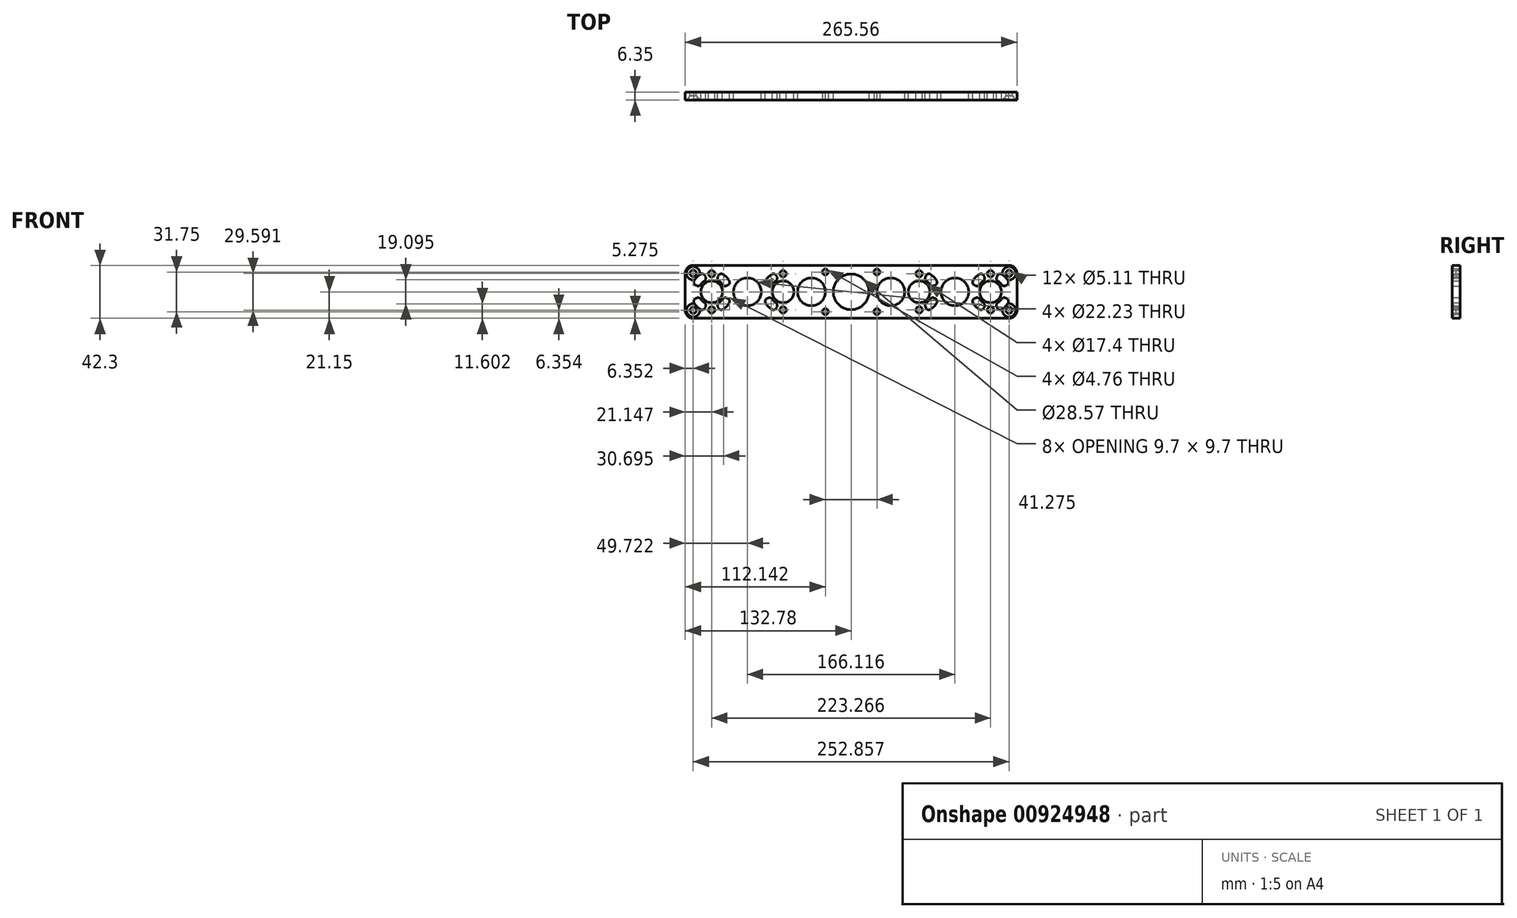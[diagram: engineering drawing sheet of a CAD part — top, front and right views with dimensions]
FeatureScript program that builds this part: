
annotation { "Feature Type Name" : "Feature", "Feature Type Description" : "" }
export const myFeature = defineFeature(function(context is Context, id is Id, definition is map)
    precondition{}
    {
        {
            var Q0;
            Q0=qCreatedBy(makeId("Front.planeOp"),FACE);
            var sketch = newSketch(context, id + "F0", { "sketchPlane" : qUnion([Q0])});
            skLineSegment(sketch, "E0.bottom", {"start": v(-139.7, 25.4) * mm, "end": v(139.7, 25.4) * mm, "construction": true});
            skLineSegment(sketch, "E0.top", {"start": v(-139.7, -25.4) * mm, "end": v(139.7, -25.4) * mm, "construction": true});
            skLineSegment(sketch, "E0.left", {"start": v(-139.7, 25.4) * mm, "end": v(-139.7, -25.4) * mm, "construction": true});
            skLineSegment(sketch, "E0.right", {"start": v(139.7, 25.4) * mm, "end": v(139.7, -25.4) * mm, "construction": true});
            skPoint(sketch, "E0.middle", {"position": v(0, 0) * mm});
            skCircle(sketch, "E1", {"center": v(-111.63, 0) * mm, "radius": 21.15 * mm, "construction": true});
            skCircle(sketch, "E2", {"center": v(-54.48, 0) * mm, "radius": 21.15 * mm, "construction": true});
            skCircle(sketch, "E3", {"center": v(-111.63, 0) * mm, "radius": 4.76 * mm, "construction": true});
            skCircle(sketch, "E4", {"center": v(-83.06, 0) * mm, "radius": 23.81 * mm, "construction": true});
            skCircle(sketch, "E5", {"center": v(-54.48, 0) * mm, "radius": 4.76 * mm, "construction": true});
            skCircle(sketch, "E6", {"center": v(-83.06, 0) * mm, "radius": 19.09 * mm, "construction": true});
            skCircle(sketch, "E7", {"center": v(-31.75, 0) * mm, "radius": 19.09 * mm, "construction": true});
            skCircle(sketch, "E8", {"center": v(-83.06, 0) * mm, "radius": 11.11 * mm});
            skCircle(sketch, "E9", {"center": v(-31.75, 0) * mm, "radius": 8.9 * mm, "construction": true});
            skCircle(sketch, "E10", {"center": v(0, 0) * mm, "radius": 22.86 * mm, "construction": true});
            skLineSegment(sketch, "E11", {"start": v(0, 25.4) * mm, "end": v(0, -25.4) * mm, "construction": true});
            skCircle(sketch, "E12.MirrorC", {"center": v(54.48, 0) * mm, "radius": 21.15 * mm, "construction": true});
            skCircle(sketch, "E13.MirrorC", {"center": v(111.63, 0) * mm, "radius": 21.15 * mm, "construction": true});
            skCircle(sketch, "E14.MirrorC", {"center": v(111.63, 0) * mm, "radius": 4.76 * mm, "construction": true});
            skCircle(sketch, "E15.MirrorC", {"center": v(83.06, 0) * mm, "radius": 19.09 * mm, "construction": true});
            skCircle(sketch, "E16.MirrorC", {"center": v(83.06, 0) * mm, "radius": 11.11 * mm});
            skCircle(sketch, "E17.MirrorC", {"center": v(54.48, 0) * mm, "radius": 4.76 * mm, "construction": true});
            skCircle(sketch, "E18.MirrorC", {"center": v(83.06, 0) * mm, "radius": 23.81 * mm, "construction": true});
            skCircle(sketch, "E19.MirrorC", {"center": v(31.75, 0) * mm, "radius": 19.09 * mm, "construction": true});
            skCircle(sketch, "E20.MirrorC", {"center": v(31.75, 0) * mm, "radius": 8.9 * mm, "construction": true});
            skLineSegment(sketch, "E21", {"start": v(-111.63, 14.5) * mm, "end": v(-111.63, 0) * mm, "construction": true});
            skLineSegment(sketch, "E22", {"start": v(-111.63, 0) * mm, "end": v(-111.63, -14.5) * mm, "construction": true});
            skCircle(sketch, "E23", {"center": v(-111.63, 14.5) * mm, "radius": 2.55 * mm});
            skCircle(sketch, "E24", {"center": v(-111.63, -14.5) * mm, "radius": 2.55 * mm});
            skCircle(sketch, "E25", {"center": v(-111.63, 0) * mm, "radius": 8.7 * mm});
            skLineSegment(sketch, "E26", {"start": v(-54.48, -14.5) * mm, "end": v(-54.48, 0) * mm, "construction": true});
            skLineSegment(sketch, "E27", {"start": v(-54.48, 0) * mm, "end": v(-54.48, 14.5) * mm, "construction": true});
            skCircle(sketch, "E28", {"center": v(-54.48, 14.5) * mm, "radius": 2.55 * mm});
            skCircle(sketch, "E29", {"center": v(-54.48, -14.5) * mm, "radius": 2.55 * mm});
            skCircle(sketch, "E30", {"center": v(-54.48, 0) * mm, "radius": 8.7 * mm});
            skLineSegment(sketch, "E31.MirrorCS", {"start": v(54.48, 0) * mm, "end": v(54.48, 14.5) * mm, "construction": true});
            skCircle(sketch, "E32.MirrorC", {"center": v(54.48, 14.5) * mm, "radius": 2.55 * mm});
            skLineSegment(sketch, "E33.MirrorCS", {"start": v(54.48, -14.5) * mm, "end": v(54.48, 0) * mm, "construction": true});
            skCircle(sketch, "E34.MirrorC", {"center": v(54.48, -14.5) * mm, "radius": 2.55 * mm});
            skCircle(sketch, "E35.MirrorC", {"center": v(54.48, 0) * mm, "radius": 8.7 * mm});
            skCircle(sketch, "E36.MirrorC", {"center": v(111.63, 0) * mm, "radius": 8.7 * mm});
            skLineSegment(sketch, "E37.MirrorCS", {"start": v(111.63, 0) * mm, "end": v(111.63, -14.5) * mm, "construction": true});
            skCircle(sketch, "E38.MirrorC", {"center": v(111.63, -14.5) * mm, "radius": 2.55 * mm});
            skLineSegment(sketch, "E39.MirrorCS", {"start": v(111.63, 14.5) * mm, "end": v(111.63, 0) * mm, "construction": true});
            skCircle(sketch, "E40.MirrorC", {"center": v(111.63, 14.5) * mm, "radius": 2.55 * mm});
            skCircle(sketch, "E41", {"center": v(-31.75, 0) * mm, "radius": 11.11 * mm});
            skCircle(sketch, "E42", {"center": v(31.75, 0) * mm, "radius": 11.11 * mm});
            skCircle(sketch, "E43", {"center": v(0, 0) * mm, "radius": 14.29 * mm});
            skArc(sketch, "E44", {"start": v(-111.63, 21.15) * mm, "mid": v(-132.78, 0) * mm, "end": v(-111.63, -21.15) * mm, "construction": true});
            skLineSegment(sketch, "E45", {"start": v(-111.63, 21.15) * mm, "end": v(111.63, 21.15) * mm});
            skArc(sketch, "E46", {"start": v(111.63, 21.15) * mm, "mid": v(132.78, 0) * mm, "end": v(111.63, -21.15) * mm, "construction": true});
            skLineSegment(sketch, "E47", {"start": v(111.63, -21.15) * mm, "end": v(-111.63, -21.15) * mm});
            skLineSegment(sketch, "E48", {"start": v(111.63, 21.15) * mm, "end": v(126.43, 21.15) * mm});
            skPoint(sketch, "E48.endSnap0", {"position": v(132.78, 0) * mm});
            skLineSegment(sketch, "E49", {"start": v(132.78, 14.8) * mm, "end": v(132.78, -14.8) * mm});
            skLineSegment(sketch, "E50", {"start": v(126.43, -21.15) * mm, "end": v(111.63, -21.15) * mm});
            skCircle(sketch, "E51", {"center": v(126.43, 14.8) * mm, "radius": 6.35 * mm, "construction": true});
            skCircle(sketch, "E52", {"center": v(126.43, 14.8) * mm, "radius": 2.55 * mm});
            skLineSegment(sketch, "E53", {"start": v(-111.63, -21.15) * mm, "end": v(-126.43, -21.15) * mm});
            skPoint(sketch, "E53.endSnap0", {"position": v(-132.78, 0) * mm});
            skLineSegment(sketch, "E54", {"start": v(-132.78, -14.8) * mm, "end": v(-132.78, 14.8) * mm});
            skLineSegment(sketch, "E55", {"start": v(-126.43, 21.15) * mm, "end": v(-111.63, 21.15) * mm});
            skPoint(sketch, "E56.visualSharp", {"position": v(132.78, 21.15) * mm});
            skArc(sketch, "E56.filletArc", {"start": v(132.78, 14.8) * mm, "mid": v(130.92, 19.29) * mm, "end": v(126.43, 21.15) * mm});
            skPoint(sketch, "E57.visualSharp", {"position": v(132.78, -21.15) * mm});
            skArc(sketch, "E57.filletArc", {"start": v(126.43, -21.15) * mm, "mid": v(130.92, -19.29) * mm, "end": v(132.78, -14.8) * mm});
            skPoint(sketch, "E58.visualSharp", {"position": v(-132.78, -21.15) * mm});
            skArc(sketch, "E58.filletArc", {"start": v(-132.78, -14.8) * mm, "mid": v(-130.92, -19.29) * mm, "end": v(-126.43, -21.15) * mm});
            skPoint(sketch, "E59.visualSharp", {"position": v(-132.78, 21.15) * mm});
            skArc(sketch, "E59.filletArc", {"start": v(-126.43, 21.15) * mm, "mid": v(-130.92, 19.29) * mm, "end": v(-132.78, 14.8) * mm});
            skCircle(sketch, "E60", {"center": v(-126.43, 14.8) * mm, "radius": 6.35 * mm, "construction": true});
            skCircle(sketch, "E61", {"center": v(126.43, -14.8) * mm, "radius": 6.35 * mm, "construction": true});
            skCircle(sketch, "E62", {"center": v(126.43, -14.8) * mm, "radius": 2.55 * mm});
            skCircle(sketch, "E63", {"center": v(-126.43, -14.8) * mm, "radius": 6.35 * mm, "construction": true});
            skCircle(sketch, "E64", {"center": v(-126.43, -14.8) * mm, "radius": 2.55 * mm});
            skCircle(sketch, "E65", {"center": v(-126.43, 14.8) * mm, "radius": 2.55 * mm});
            skSolve(sketch);
        }
        {
            var Q0;
            Q0=qSketchRegion(id+"F0",true);
            extrude(context, id + "F1", {"entities" : qUnion([Q0]), "depth" : 6.35 * mm, "offsetDistance" : 25.4 * mm});
        }
        {
            var Q0;
            Q0=makeQuery(id+"F1.opExtrude","CAP_FACE",FACE,{"disambiguationData":[OSD([sQuery(id+"F0.wireOp",EDGE,"E8"),sQuery(id+"F0.wireOp",EDGE,"E16.MirrorC"),sQuery(id+"F0.wireOp",EDGE,"E23"),sQuery(id+"F0.wireOp",EDGE,"E24"),sQuery(id+"F0.wireOp",EDGE,"E25"),sQuery(id+"F0.wireOp",EDGE,"E28"),sQuery(id+"F0.wireOp",EDGE,"E29"),sQuery(id+"F0.wireOp",EDGE,"E30"),sQuery(id+"F0.wireOp",EDGE,"E32.MirrorC"),sQuery(id+"F0.wireOp",EDGE,"E34.MirrorC"),sQuery(id+"F0.wireOp",EDGE,"E35.MirrorC"),sQuery(id+"F0.wireOp",EDGE,"E36.MirrorC"),sQuery(id+"F0.wireOp",EDGE,"E38.MirrorC"),sQuery(id+"F0.wireOp",EDGE,"E40.MirrorC"),sQuery(id+"F0.wireOp",EDGE,"E41"),sQuery(id+"F0.wireOp",EDGE,"E42"),sQuery(id+"F0.wireOp",EDGE,"E43"),sQuery(id+"F0.wireOp",EDGE,"E44"),sQuery(id+"F0.wireOp",EDGE,"E45"),sQuery(id+"F0.wireOp",EDGE,"E46"),sQuery(id+"F0.wireOp",EDGE,"E47")])],"isStart":false});
            var sketch = newSketch(context, id + "F2", { "sketchPlane" : qUnion([Q0])});
            skLineSegment(sketch, "E66.bottom", {"start": v(20.64, 15.88) * mm, "end": v(-20.64, 15.88) * mm, "construction": true});
            skLineSegment(sketch, "E66.top", {"start": v(20.64, -15.88) * mm, "end": v(-20.64, -15.88) * mm, "construction": true});
            skLineSegment(sketch, "E66.left", {"start": v(20.64, 15.88) * mm, "end": v(20.64, -15.88) * mm, "construction": true});
            skLineSegment(sketch, "E66.right", {"start": v(-20.64, 15.88) * mm, "end": v(-20.64, -15.88) * mm, "construction": true});
            skPoint(sketch, "E66.middle", {"position": v(0, 0) * mm});
            skCircle(sketch, "E67", {"center": v(20.64, 15.88) * mm, "radius": 2.38 * mm});
            skCircle(sketch, "E68", {"center": v(20.64, -15.88) * mm, "radius": 2.38 * mm});
            skCircle(sketch, "E69", {"center": v(-20.64, -15.88) * mm, "radius": 2.38 * mm});
            skCircle(sketch, "E70", {"center": v(-20.64, 15.88) * mm, "radius": 2.38 * mm});
            skSolve(sketch);
        }
        {
            var Q0;
            Q0=qSketchRegion(id+"F2",true);
            extrude(context, id + "F3", {"entities" : qUnion([Q0]), "operationType" : NewBodyOperationType.REMOVE, "endBound" : BoundingType.THROUGH_ALL, "oppositeDirection" : true, "depth" : 25.4 * mm, "offsetDistance" : 25.4 * mm});
        }
        {
            var Q0;
            Q0=makeQuery(id+"F1.opExtrude","SWEPT_FACE",FACE,{"disambiguationData":[OSD([sQuery(id+"F0.wireOp",EDGE,"E49")])]});
            cPlane(context, id + "F4", {"entities" : qUnion([Q0]), "cplaneType" : CPlaneType.OFFSET, "offset" : 6.35 * mm, "oppositeDirection" : true, "width" : 152.4 * mm, "height" : 152.4 * mm});
        }
        {
            var Q0;
            Q0=qCreatedBy(id+"F4.planeOp",FACE);
            var sketch = newSketch(context, id + "F5", { "sketchPlane" : qUnion([Q0])});
            skLineSegment(sketch, "E71", {"start": v(-6.35, 14.8) * mm, "end": v(-3.12, 14.8) * mm});
            skLineSegment(sketch, "E72", {"start": v(-3.12, 14.8) * mm, "end": v(-3.12, 17.34) * mm});
            skLineSegment(sketch, "E73", {"start": v(-3.12, 17.34) * mm, "end": v(-6.35, 20.14) * mm});
            skLineSegment(sketch, "E74", {"start": v(-6.35, 20.14) * mm, "end": v(-6.35, 14.8) * mm});
            skLineSegment(sketch, "E75", {"start": v(-3.12, 14.8) * mm, "end": v(-3.12, 12.26) * mm, "construction": true});
            skLineSegment(sketch, "E76", {"start": v(-3.12, 12.26) * mm, "end": v(-6.35, 9.45) * mm, "construction": true});
            skLineSegment(sketch, "E77", {"start": v(-6.35, 9.45) * mm, "end": v(-6.35, 14.8) * mm, "construction": true});
            skSolve(sketch);
        }
        {
            var Q0;
            Q0 = qSketchRegion(id + "F5", true);
            var Q1;
            Q1=sQuery(id+"F5.wireOp",EDGE,"E71");
            revolve(context, id + "F6", {"operationType" : NewBodyOperationType.REMOVE, "surfaceOperationType" : NewSurfaceOperationType.NEW, "entities" : qUnion([Q0]), "axis" : qUnion([Q1]), "revolveType" : RevolveType.FULL, "oppositeDirection" : true});
        }
        {
            var Q0;
            Q0=qCreatedBy(id+"F4.planeOp",FACE);
            var sketch = newSketch(context, id + "F7", { "sketchPlane" : qUnion([Q0])});
            skLineSegment(sketch, "E78", {"start": v(-6.35, -14.8) * mm, "end": v(-3.12, -14.8) * mm});
            skLineSegment(sketch, "E79", {"start": v(-3.12, -14.8) * mm, "end": v(-3.12, -12.26) * mm});
            skLineSegment(sketch, "E80", {"start": v(-3.12, -12.26) * mm, "end": v(-6.35, -9.45) * mm});
            skLineSegment(sketch, "E81", {"start": v(-6.35, -9.45) * mm, "end": v(-6.35, -14.8) * mm});
            skLineSegment(sketch, "E82", {"start": v(-3.12, -14.8) * mm, "end": v(-3.12, -17.34) * mm, "construction": true});
            skLineSegment(sketch, "E83", {"start": v(-3.12, -17.34) * mm, "end": v(-6.35, -20.14) * mm, "construction": true});
            skLineSegment(sketch, "E84", {"start": v(-6.35, -20.14) * mm, "end": v(-6.35, -14.8) * mm, "construction": true});
            skSolve(sketch);
        }
        {
            var Q0;
            Q0 = qSketchRegion(id + "F7", true);
            var Q1;
            Q1=sQuery(id+"F7.wireOp",EDGE,"E78");
            revolve(context, id + "F8", {"operationType" : NewBodyOperationType.REMOVE, "surfaceOperationType" : NewSurfaceOperationType.NEW, "entities" : qUnion([Q0]), "axis" : qUnion([Q1]), "revolveType" : RevolveType.FULL, "oppositeDirection" : true});
        }
        {
            var Q0;
            Q0=makeQuery(id+"F1.opExtrude","SWEPT_FACE",FACE,{"disambiguationData":[OSD([sQuery(id+"F0.wireOp",EDGE,"E54")])]});
            cPlane(context, id + "F9", {"entities" : qUnion([Q0]), "cplaneType" : CPlaneType.OFFSET, "offset" : 6.35 * mm, "oppositeDirection" : true, "width" : 152.4 * mm, "height" : 152.4 * mm});
        }
        {
            var Q0;
            Q0=qCreatedBy(id+"F9.planeOp",FACE);
            var sketch = newSketch(context, id + "F10", { "sketchPlane" : qUnion([Q0])});
            skLineSegment(sketch, "E85", {"start": v(6.35, 14.8) * mm, "end": v(3.12, 14.8) * mm});
            skLineSegment(sketch, "E86", {"start": v(3.12, 14.8) * mm, "end": v(3.12, 12.26) * mm});
            skLineSegment(sketch, "E87", {"start": v(3.12, 12.26) * mm, "end": v(6.35, 9.45) * mm});
            skLineSegment(sketch, "E88", {"start": v(6.35, 9.45) * mm, "end": v(6.35, 14.8) * mm});
            skLineSegment(sketch, "E89", {"start": v(3.12, 14.8) * mm, "end": v(3.12, 17.34) * mm, "construction": true});
            skLineSegment(sketch, "E90", {"start": v(3.12, 17.34) * mm, "end": v(6.35, 20.14) * mm, "construction": true});
            skLineSegment(sketch, "E91", {"start": v(6.35, 20.14) * mm, "end": v(6.35, 14.8) * mm, "construction": true});
            skSolve(sketch);
        }
        {
            var Q0;
            Q0 = qSketchRegion(id + "F10", true);
            var Q1;
            Q1=sQuery(id+"F10.wireOp",EDGE,"E85");
            revolve(context, id + "F11", {"operationType" : NewBodyOperationType.REMOVE, "surfaceOperationType" : NewSurfaceOperationType.NEW, "entities" : qUnion([Q0]), "axis" : qUnion([Q1]), "revolveType" : RevolveType.FULL, "oppositeDirection" : true});
        }
        {
            var Q0;
            Q0=qCreatedBy(id+"F9.planeOp",FACE);
            var sketch = newSketch(context, id + "F12", { "sketchPlane" : qUnion([Q0])});
            skLineSegment(sketch, "E92", {"start": v(6.35, -14.8) * mm, "end": v(3.12, -14.8) * mm});
            skLineSegment(sketch, "E93", {"start": v(3.12, -14.8) * mm, "end": v(3.12, -17.34) * mm});
            skLineSegment(sketch, "E94", {"start": v(3.12, -17.34) * mm, "end": v(6.35, -20.14) * mm});
            skLineSegment(sketch, "E95", {"start": v(6.35, -20.14) * mm, "end": v(6.35, -14.8) * mm});
            skLineSegment(sketch, "E96", {"start": v(3.12, -14.8) * mm, "end": v(3.12, -12.26) * mm, "construction": true});
            skLineSegment(sketch, "E97", {"start": v(3.12, -12.26) * mm, "end": v(6.35, -9.45) * mm, "construction": true});
            skLineSegment(sketch, "E98", {"start": v(6.35, -9.45) * mm, "end": v(6.35, -14.8) * mm, "construction": true});
            skSolve(sketch);
        }
        {
            var Q0;
            Q0 = qSketchRegion(id + "F12", true);
            var Q1;
            Q1=sQuery(id+"F12.wireOp",EDGE,"E92");
            revolve(context, id + "F13", {"operationType" : NewBodyOperationType.REMOVE, "surfaceOperationType" : NewSurfaceOperationType.NEW, "entities" : qUnion([Q0]), "axis" : qUnion([Q1]), "revolveType" : RevolveType.FULL});
        }
        {
            var Q0;
            Q0=makeQuery(id+"F1.opExtrude","CAP_FACE",FACE,{"disambiguationData":[OSD([sQuery(id+"F0.wireOp",EDGE,"E8"),sQuery(id+"F0.wireOp",EDGE,"E16.MirrorC"),sQuery(id+"F0.wireOp",EDGE,"E23"),sQuery(id+"F0.wireOp",EDGE,"E24"),sQuery(id+"F0.wireOp",EDGE,"E25"),sQuery(id+"F0.wireOp",EDGE,"E28"),sQuery(id+"F0.wireOp",EDGE,"E29"),sQuery(id+"F0.wireOp",EDGE,"E30"),sQuery(id+"F0.wireOp",EDGE,"E32.MirrorC"),sQuery(id+"F0.wireOp",EDGE,"E34.MirrorC"),sQuery(id+"F0.wireOp",EDGE,"E35.MirrorC"),sQuery(id+"F0.wireOp",EDGE,"E36.MirrorC"),sQuery(id+"F0.wireOp",EDGE,"E38.MirrorC"),sQuery(id+"F0.wireOp",EDGE,"E40.MirrorC"),sQuery(id+"F0.wireOp",EDGE,"E41"),sQuery(id+"F0.wireOp",EDGE,"E42"),sQuery(id+"F0.wireOp",EDGE,"E43"),sQuery(id+"F0.wireOp",EDGE,"E45"),sQuery(id+"F0.wireOp",EDGE,"E47"),sQuery(id+"F0.wireOp",EDGE,"E48"),sQuery(id+"F0.wireOp",EDGE,"E49"),sQuery(id+"F0.wireOp",EDGE,"E50"),sQuery(id+"F0.wireOp",EDGE,"E52"),sQuery(id+"F0.wireOp",EDGE,"E53"),sQuery(id+"F0.wireOp",EDGE,"E54"),sQuery(id+"F0.wireOp",EDGE,"E55"),sQuery(id+"F0.wireOp",EDGE,"E56.filletArc"),sQuery(id+"F0.wireOp",EDGE,"E57.filletArc"),sQuery(id+"F0.wireOp",EDGE,"E58.filletArc"),sQuery(id+"F0.wireOp",EDGE,"E59.filletArc"),sQuery(id+"F0.wireOp",EDGE,"E62"),sQuery(id+"F0.wireOp",EDGE,"E64"),sQuery(id+"F0.wireOp",EDGE,"E65")])],"isStart":true});
            var sketch = newSketch(context, id + "F14", { "sketchPlane" : qUnion([Q0])});
            skCircle(sketch, "E99", {"center": v(111.63, 0) * mm, "radius": 10.48 * mm, "construction": true});
            skCircle(sketch, "E100", {"center": v(111.63, 0) * mm, "radius": 16.67 * mm, "construction": true});
            skLineSegment(sketch, "E101", {"start": v(118.01, 15.4) * mm, "end": v(105.25, -15.4) * mm, "construction": true});
            skLineSegment(sketch, "E102", {"start": v(105.25, 15.4) * mm, "end": v(118.01, -15.4) * mm, "construction": true});
            skLineSegment(sketch, "E103", {"start": v(96.23, 6.38) * mm, "end": v(127.03, -6.38) * mm, "construction": true});
            skLineSegment(sketch, "E104", {"start": v(127.03, 6.38) * mm, "end": v(96.23, -6.38) * mm, "construction": true});
            skLineSegment(sketch, "E105", {"start": v(94.96, 0) * mm, "end": v(128.3, 0) * mm, "construction": true});
            skLineSegment(sketch, "E106", {"start": v(106.75, -11.8) * mm, "end": v(106.31, -12.84) * mm});
            skLineSegment(sketch, "E107", {"start": v(99.84, -4.89) * mm, "end": v(98.8, -5.32) * mm});
            skLineSegment(sketch, "E108", {"start": v(99.84, 4.89) * mm, "end": v(98.8, 5.32) * mm});
            skLineSegment(sketch, "E109", {"start": v(106.75, 11.8) * mm, "end": v(106.31, 12.84) * mm});
            skLineSegment(sketch, "E110", {"start": v(116.52, 11.8) * mm, "end": v(116.95, 12.84) * mm});
            skLineSegment(sketch, "E111", {"start": v(123.43, 4.89) * mm, "end": v(124.47, 5.32) * mm});
            skLineSegment(sketch, "E112", {"start": v(122.11, 0) * mm, "end": v(128.3, 0) * mm});
            skLineSegment(sketch, "E113", {"start": v(123.43, -4.89) * mm, "end": v(124.47, -5.32) * mm});
            skLineSegment(sketch, "E114", {"start": v(116.52, -11.8) * mm, "end": v(116.95, -12.84) * mm});
            skArc(sketch, "E115", {"start": v(120.68, -14) * mm, "mid": v(123.42, -11.79) * mm, "end": v(125.64, -9.04) * mm});
            skArc(sketch, "E116", {"start": v(125.64, 9.04) * mm, "mid": v(123.42, 11.79) * mm, "end": v(120.68, 14) * mm});
            skArc(sketch, "E117", {"start": v(102.59, 14) * mm, "mid": v(99.85, 11.79) * mm, "end": v(97.63, 9.04) * mm});
            skArc(sketch, "E118", {"start": v(97.63, -9.04) * mm, "mid": v(99.85, -11.79) * mm, "end": v(102.59, -14) * mm});
            skArc(sketch, "E119", {"start": v(120.34, -5.82) * mm, "mid": v(119.04, -7.4) * mm, "end": v(117.45, -8.71) * mm});
            skArc(sketch, "E120", {"start": v(105.81, -8.71) * mm, "mid": v(104.22, -7.4) * mm, "end": v(102.92, -5.82) * mm});
            skArc(sketch, "E121", {"start": v(102.92, 5.82) * mm, "mid": v(104.22, 7.4) * mm, "end": v(105.81, 8.71) * mm});
            skArc(sketch, "E122", {"start": v(117.45, 8.71) * mm, "mid": v(119.04, 7.4) * mm, "end": v(120.34, 5.82) * mm});
            skPoint(sketch, "E123.visualSharp", {"position": v(115.64, -9.68) * mm});
            skArc(sketch, "E123.filletArc", {"start": v(117.45, -8.71) * mm, "mid": v(116.43, -10.09) * mm, "end": v(116.52, -11.8) * mm});
            skPoint(sketch, "E124.visualSharp", {"position": v(118.01, -15.4) * mm});
            skArc(sketch, "E124.filletArc", {"start": v(116.95, -12.84) * mm, "mid": v(118.54, -14.3) * mm, "end": v(120.68, -14) * mm});
            skPoint(sketch, "E125.visualSharp", {"position": v(127.03, -6.38) * mm});
            skArc(sketch, "E125.filletArc", {"start": v(125.64, -9.04) * mm, "mid": v(125.93, -6.9) * mm, "end": v(124.47, -5.32) * mm});
            skPoint(sketch, "E126.visualSharp", {"position": v(121.31, -4) * mm});
            skArc(sketch, "E126.filletArc", {"start": v(123.43, -4.89) * mm, "mid": v(121.72, -4.8) * mm, "end": v(120.34, -5.82) * mm});
            skPoint(sketch, "E127.visualSharp", {"position": v(121.31, 4) * mm});
            skArc(sketch, "E127.filletArc", {"start": v(120.34, 5.82) * mm, "mid": v(121.72, 4.8) * mm, "end": v(123.43, 4.89) * mm});
            skPoint(sketch, "E128.visualSharp", {"position": v(127.03, 6.38) * mm});
            skArc(sketch, "E128.filletArc", {"start": v(124.47, 5.32) * mm, "mid": v(125.93, 6.9) * mm, "end": v(125.64, 9.04) * mm});
            skPoint(sketch, "E129.visualSharp", {"position": v(118.01, 15.4) * mm});
            skArc(sketch, "E129.filletArc", {"start": v(120.68, 14) * mm, "mid": v(118.54, 14.3) * mm, "end": v(116.95, 12.84) * mm});
            skPoint(sketch, "E130.visualSharp", {"position": v(115.64, 9.68) * mm});
            skArc(sketch, "E130.filletArc", {"start": v(116.52, 11.8) * mm, "mid": v(116.43, 10.09) * mm, "end": v(117.45, 8.71) * mm});
            skPoint(sketch, "E131.visualSharp", {"position": v(107.62, 9.68) * mm});
            skArc(sketch, "E131.filletArc", {"start": v(105.81, 8.71) * mm, "mid": v(106.83, 10.09) * mm, "end": v(106.75, 11.8) * mm});
            skPoint(sketch, "E132.visualSharp", {"position": v(105.25, 15.4) * mm});
            skArc(sketch, "E132.filletArc", {"start": v(106.31, 12.84) * mm, "mid": v(104.72, 14.3) * mm, "end": v(102.59, 14) * mm});
            skPoint(sketch, "E133.visualSharp", {"position": v(96.23, 6.38) * mm});
            skArc(sketch, "E133.filletArc", {"start": v(97.63, 9.04) * mm, "mid": v(97.34, 6.9) * mm, "end": v(98.8, 5.32) * mm});
            skPoint(sketch, "E134.visualSharp", {"position": v(101.95, 4) * mm});
            skArc(sketch, "E134.filletArc", {"start": v(99.84, 4.89) * mm, "mid": v(101.55, 4.8) * mm, "end": v(102.92, 5.82) * mm});
            skPoint(sketch, "E135.visualSharp", {"position": v(101.95, -4) * mm});
            skArc(sketch, "E135.filletArc", {"start": v(102.92, -5.82) * mm, "mid": v(101.55, -4.8) * mm, "end": v(99.84, -4.89) * mm});
            skPoint(sketch, "E136.visualSharp", {"position": v(107.62, -9.68) * mm});
            skArc(sketch, "E136.filletArc", {"start": v(106.75, -11.8) * mm, "mid": v(106.83, -10.09) * mm, "end": v(105.81, -8.71) * mm});
            skPoint(sketch, "E137.visualSharp", {"position": v(105.25, -15.4) * mm});
            skArc(sketch, "E137.filletArc", {"start": v(102.59, -14) * mm, "mid": v(104.72, -14.3) * mm, "end": v(106.31, -12.84) * mm});
            skPoint(sketch, "E138.visualSharp", {"position": v(96.23, -6.38) * mm});
            skArc(sketch, "E138.filletArc", {"start": v(98.8, -5.32) * mm, "mid": v(97.34, -6.9) * mm, "end": v(97.63, -9.04) * mm});
            skLineSegment(sketch, "E139", {"start": v(54.48, -14.5) * mm, "end": v(54.48, 14.5) * mm, "construction": true});
            skLineSegment(sketch, "E140", {"start": v(-54.48, -14.5) * mm, "end": v(-54.48, 14.5) * mm, "construction": true});
            skLineSegment(sketch, "E141", {"start": v(-111.63, 14.5) * mm, "end": v(-111.63, -14.5) * mm, "construction": true});
            skCircle(sketch, "E142", {"center": v(54.48, 0) * mm, "radius": 10.48 * mm, "construction": true});
            skCircle(sketch, "E143", {"center": v(54.48, 0) * mm, "radius": 16.67 * mm, "construction": true});
            skLineSegment(sketch, "E144", {"start": v(60.86, 15.4) * mm, "end": v(48.1, -15.4) * mm, "construction": true});
            skLineSegment(sketch, "E145", {"start": v(48.1, 15.4) * mm, "end": v(60.86, -15.4) * mm, "construction": true});
            skLineSegment(sketch, "E146", {"start": v(39.08, 6.38) * mm, "end": v(69.88, -6.38) * mm, "construction": true});
            skLineSegment(sketch, "E147", {"start": v(69.88, 6.38) * mm, "end": v(39.08, -6.38) * mm, "construction": true});
            skLineSegment(sketch, "E148", {"start": v(37.81, 0) * mm, "end": v(71.15, 0) * mm, "construction": true});
            skLineSegment(sketch, "E149", {"start": v(49.6, -11.8) * mm, "end": v(49.16, -12.84) * mm, "construction": true});
            skLineSegment(sketch, "E150", {"start": v(42.69, -4.89) * mm, "end": v(41.64, -5.32) * mm, "construction": true});
            skLineSegment(sketch, "E151", {"start": v(42.69, 4.89) * mm, "end": v(41.64, 5.32) * mm, "construction": true});
            skLineSegment(sketch, "E152", {"start": v(49.6, 11.8) * mm, "end": v(49.16, 12.84) * mm, "construction": true});
            skLineSegment(sketch, "E153", {"start": v(59.37, 11.8) * mm, "end": v(59.8, 12.84) * mm});
            skLineSegment(sketch, "E154", {"start": v(66.28, 4.89) * mm, "end": v(67.32, 5.32) * mm});
            skLineSegment(sketch, "E155", {"start": v(64.96, 0) * mm, "end": v(71.15, 0) * mm});
            skLineSegment(sketch, "E156", {"start": v(66.28, -4.89) * mm, "end": v(67.32, -5.32) * mm});
            skLineSegment(sketch, "E157", {"start": v(59.37, -11.8) * mm, "end": v(59.8, -12.84) * mm});
            skArc(sketch, "E158", {"start": v(63.53, -14) * mm, "mid": v(66.27, -11.79) * mm, "end": v(68.49, -9.04) * mm});
            skArc(sketch, "E159", {"start": v(68.49, 9.04) * mm, "mid": v(66.27, 11.79) * mm, "end": v(63.53, 14) * mm});
            skArc(sketch, "E160", {"start": v(45.44, 14) * mm, "mid": v(42.7, 11.79) * mm, "end": v(40.48, 9.04) * mm, "construction": true});
            skArc(sketch, "E161", {"start": v(40.48, -9.04) * mm, "mid": v(42.7, -11.79) * mm, "end": v(45.44, -14) * mm, "construction": true});
            skArc(sketch, "E162", {"start": v(63.2, -5.82) * mm, "mid": v(61.9, -7.4) * mm, "end": v(60.3, -8.71) * mm});
            skArc(sketch, "E163", {"start": v(48.66, -8.71) * mm, "mid": v(47.07, -7.4) * mm, "end": v(45.77, -5.82) * mm, "construction": true});
            skArc(sketch, "E164", {"start": v(45.77, 5.82) * mm, "mid": v(47.07, 7.4) * mm, "end": v(48.66, 8.71) * mm, "construction": true});
            skArc(sketch, "E165", {"start": v(60.3, 8.71) * mm, "mid": v(61.9, 7.4) * mm, "end": v(63.2, 5.82) * mm});
            skPoint(sketch, "E166.visualSharp", {"position": v(58.5, -9.68) * mm});
            skArc(sketch, "E166.filletArc", {"start": v(60.3, -8.71) * mm, "mid": v(59.28, -10.09) * mm, "end": v(59.37, -11.8) * mm});
            skPoint(sketch, "E167.visualSharp", {"position": v(60.86, -15.4) * mm});
            skArc(sketch, "E167.filletArc", {"start": v(59.8, -12.84) * mm, "mid": v(61.4, -14.3) * mm, "end": v(63.53, -14) * mm});
            skPoint(sketch, "E168.visualSharp", {"position": v(69.88, -6.38) * mm});
            skArc(sketch, "E168.filletArc", {"start": v(68.49, -9.04) * mm, "mid": v(68.78, -6.9) * mm, "end": v(67.32, -5.32) * mm});
            skPoint(sketch, "E169.visualSharp", {"position": v(64.16, -4) * mm});
            skArc(sketch, "E169.filletArc", {"start": v(66.28, -4.89) * mm, "mid": v(64.57, -4.8) * mm, "end": v(63.2, -5.82) * mm});
            skPoint(sketch, "E170.visualSharp", {"position": v(64.16, 4) * mm});
            skArc(sketch, "E170.filletArc", {"start": v(63.2, 5.82) * mm, "mid": v(64.57, 4.8) * mm, "end": v(66.28, 4.89) * mm});
            skPoint(sketch, "E171.visualSharp", {"position": v(69.88, 6.38) * mm});
            skArc(sketch, "E171.filletArc", {"start": v(67.32, 5.32) * mm, "mid": v(68.78, 6.9) * mm, "end": v(68.49, 9.04) * mm});
            skPoint(sketch, "E172.visualSharp", {"position": v(60.86, 15.4) * mm});
            skArc(sketch, "E172.filletArc", {"start": v(63.53, 14) * mm, "mid": v(61.4, 14.3) * mm, "end": v(59.8, 12.84) * mm});
            skPoint(sketch, "E173.visualSharp", {"position": v(58.5, 9.68) * mm});
            skArc(sketch, "E173.filletArc", {"start": v(59.37, 11.8) * mm, "mid": v(59.28, 10.09) * mm, "end": v(60.3, 8.71) * mm});
            skPoint(sketch, "E174.visualSharp", {"position": v(50.47, 9.68) * mm});
            skArc(sketch, "E174.filletArc", {"start": v(48.66, 8.71) * mm, "mid": v(49.68, 10.09) * mm, "end": v(49.6, 11.8) * mm, "construction": true});
            skPoint(sketch, "E175.visualSharp", {"position": v(48.1, 15.4) * mm});
            skArc(sketch, "E175.filletArc", {"start": v(49.16, 12.84) * mm, "mid": v(47.57, 14.3) * mm, "end": v(45.44, 14) * mm, "construction": true});
            skPoint(sketch, "E176.visualSharp", {"position": v(39.08, 6.38) * mm});
            skArc(sketch, "E176.filletArc", {"start": v(40.48, 9.04) * mm, "mid": v(40.19, 6.9) * mm, "end": v(41.64, 5.32) * mm, "construction": true});
            skPoint(sketch, "E177.visualSharp", {"position": v(44.8, 4) * mm});
            skArc(sketch, "E177.filletArc", {"start": v(42.69, 4.89) * mm, "mid": v(44.4, 4.8) * mm, "end": v(45.77, 5.82) * mm, "construction": true});
            skPoint(sketch, "E178.visualSharp", {"position": v(44.8, -4) * mm});
            skArc(sketch, "E178.filletArc", {"start": v(45.77, -5.82) * mm, "mid": v(44.4, -4.8) * mm, "end": v(42.69, -4.89) * mm, "construction": true});
            skPoint(sketch, "E179.visualSharp", {"position": v(50.47, -9.68) * mm});
            skArc(sketch, "E179.filletArc", {"start": v(49.6, -11.8) * mm, "mid": v(49.68, -10.09) * mm, "end": v(48.66, -8.71) * mm, "construction": true});
            skPoint(sketch, "E180.visualSharp", {"position": v(48.1, -15.4) * mm});
            skArc(sketch, "E180.filletArc", {"start": v(45.44, -14) * mm, "mid": v(47.57, -14.3) * mm, "end": v(49.16, -12.84) * mm, "construction": true});
            skPoint(sketch, "E181.visualSharp", {"position": v(39.08, -6.38) * mm});
            skArc(sketch, "E181.filletArc", {"start": v(41.64, -5.32) * mm, "mid": v(40.19, -6.9) * mm, "end": v(40.48, -9.04) * mm, "construction": true});
            skCircle(sketch, "E182", {"center": v(-54.48, 0) * mm, "radius": 10.48 * mm, "construction": true});
            skCircle(sketch, "E183", {"center": v(-54.48, 0) * mm, "radius": 16.67 * mm, "construction": true});
            skLineSegment(sketch, "E184", {"start": v(-48.1, 15.4) * mm, "end": v(-60.86, -15.4) * mm, "construction": true});
            skLineSegment(sketch, "E185", {"start": v(-60.86, 15.4) * mm, "end": v(-48.1, -15.4) * mm, "construction": true});
            skLineSegment(sketch, "E186", {"start": v(-69.88, 6.38) * mm, "end": v(-39.08, -6.38) * mm, "construction": true});
            skLineSegment(sketch, "E187", {"start": v(-39.08, 6.38) * mm, "end": v(-69.88, -6.38) * mm, "construction": true});
            skLineSegment(sketch, "E188", {"start": v(-71.15, 0) * mm, "end": v(-37.81, 0) * mm, "construction": true});
            skLineSegment(sketch, "E189", {"start": v(-59.37, -11.8) * mm, "end": v(-59.8, -12.84) * mm});
            skLineSegment(sketch, "E190", {"start": v(-66.28, -4.89) * mm, "end": v(-67.32, -5.32) * mm});
            skLineSegment(sketch, "E191", {"start": v(-66.28, 4.89) * mm, "end": v(-67.32, 5.32) * mm});
            skLineSegment(sketch, "E192", {"start": v(-59.37, 11.8) * mm, "end": v(-59.8, 12.84) * mm});
            skLineSegment(sketch, "E193", {"start": v(-49.6, 11.8) * mm, "end": v(-49.16, 12.84) * mm, "construction": true});
            skLineSegment(sketch, "E194", {"start": v(-42.69, 4.89) * mm, "end": v(-41.64, 5.32) * mm, "construction": true});
            skLineSegment(sketch, "E195", {"start": v(-44, 0) * mm, "end": v(-37.81, 0) * mm, "construction": true});
            skLineSegment(sketch, "E196", {"start": v(-42.69, -4.89) * mm, "end": v(-41.64, -5.32) * mm, "construction": true});
            skLineSegment(sketch, "E197", {"start": v(-49.6, -11.8) * mm, "end": v(-49.16, -12.84) * mm, "construction": true});
            skArc(sketch, "E198", {"start": v(-45.44, -14) * mm, "mid": v(-42.7, -11.79) * mm, "end": v(-40.48, -9.04) * mm, "construction": true});
            skArc(sketch, "E199", {"start": v(-40.48, 9.04) * mm, "mid": v(-42.7, 11.79) * mm, "end": v(-45.44, 14) * mm, "construction": true});
            skArc(sketch, "E200", {"start": v(-63.53, 14) * mm, "mid": v(-66.27, 11.79) * mm, "end": v(-68.49, 9.04) * mm});
            skArc(sketch, "E201", {"start": v(-68.49, -9.04) * mm, "mid": v(-66.27, -11.79) * mm, "end": v(-63.53, -14) * mm});
            skArc(sketch, "E202", {"start": v(-45.77, -5.82) * mm, "mid": v(-47.07, -7.4) * mm, "end": v(-48.66, -8.71) * mm, "construction": true});
            skArc(sketch, "E203", {"start": v(-60.3, -8.71) * mm, "mid": v(-61.9, -7.4) * mm, "end": v(-63.2, -5.82) * mm});
            skArc(sketch, "E204", {"start": v(-63.2, 5.82) * mm, "mid": v(-61.9, 7.4) * mm, "end": v(-60.3, 8.71) * mm});
            skArc(sketch, "E205", {"start": v(-48.66, 8.71) * mm, "mid": v(-47.07, 7.4) * mm, "end": v(-45.77, 5.82) * mm, "construction": true});
            skPoint(sketch, "E206.visualSharp", {"position": v(-50.47, -9.68) * mm});
            skArc(sketch, "E206.filletArc", {"start": v(-48.66, -8.71) * mm, "mid": v(-49.68, -10.09) * mm, "end": v(-49.6, -11.8) * mm, "construction": true});
            skPoint(sketch, "E207.visualSharp", {"position": v(-48.1, -15.4) * mm});
            skArc(sketch, "E207.filletArc", {"start": v(-49.16, -12.84) * mm, "mid": v(-47.57, -14.3) * mm, "end": v(-45.44, -14) * mm, "construction": true});
            skPoint(sketch, "E208.visualSharp", {"position": v(-39.08, -6.38) * mm});
            skArc(sketch, "E208.filletArc", {"start": v(-40.48, -9.04) * mm, "mid": v(-40.19, -6.9) * mm, "end": v(-41.64, -5.32) * mm, "construction": true});
            skPoint(sketch, "E209.visualSharp", {"position": v(-44.8, -4) * mm});
            skArc(sketch, "E209.filletArc", {"start": v(-42.69, -4.89) * mm, "mid": v(-44.4, -4.8) * mm, "end": v(-45.77, -5.82) * mm, "construction": true});
            skPoint(sketch, "E210.visualSharp", {"position": v(-44.8, 4) * mm});
            skArc(sketch, "E210.filletArc", {"start": v(-45.77, 5.82) * mm, "mid": v(-44.4, 4.8) * mm, "end": v(-42.69, 4.89) * mm, "construction": true});
            skPoint(sketch, "E211.visualSharp", {"position": v(-39.08, 6.38) * mm});
            skArc(sketch, "E211.filletArc", {"start": v(-41.64, 5.32) * mm, "mid": v(-40.19, 6.9) * mm, "end": v(-40.48, 9.04) * mm, "construction": true});
            skPoint(sketch, "E212.visualSharp", {"position": v(-48.1, 15.4) * mm});
            skArc(sketch, "E212.filletArc", {"start": v(-45.44, 14) * mm, "mid": v(-47.57, 14.3) * mm, "end": v(-49.16, 12.84) * mm, "construction": true});
            skPoint(sketch, "E213.visualSharp", {"position": v(-50.47, 9.68) * mm});
            skArc(sketch, "E213.filletArc", {"start": v(-49.6, 11.8) * mm, "mid": v(-49.68, 10.09) * mm, "end": v(-48.66, 8.71) * mm, "construction": true});
            skPoint(sketch, "E214.visualSharp", {"position": v(-58.5, 9.68) * mm});
            skArc(sketch, "E214.filletArc", {"start": v(-60.3, 8.71) * mm, "mid": v(-59.28, 10.09) * mm, "end": v(-59.37, 11.8) * mm});
            skPoint(sketch, "E215.visualSharp", {"position": v(-60.86, 15.4) * mm});
            skArc(sketch, "E215.filletArc", {"start": v(-59.8, 12.84) * mm, "mid": v(-61.4, 14.3) * mm, "end": v(-63.53, 14) * mm});
            skPoint(sketch, "E216.visualSharp", {"position": v(-69.88, 6.38) * mm});
            skArc(sketch, "E216.filletArc", {"start": v(-68.49, 9.04) * mm, "mid": v(-68.78, 6.9) * mm, "end": v(-67.32, 5.32) * mm});
            skPoint(sketch, "E217.visualSharp", {"position": v(-64.16, 4) * mm});
            skArc(sketch, "E217.filletArc", {"start": v(-66.28, 4.89) * mm, "mid": v(-64.57, 4.8) * mm, "end": v(-63.2, 5.82) * mm});
            skPoint(sketch, "E218.visualSharp", {"position": v(-64.16, -4) * mm});
            skArc(sketch, "E218.filletArc", {"start": v(-63.2, -5.82) * mm, "mid": v(-64.57, -4.8) * mm, "end": v(-66.28, -4.89) * mm});
            skPoint(sketch, "E219.visualSharp", {"position": v(-58.5, -9.68) * mm});
            skArc(sketch, "E219.filletArc", {"start": v(-59.37, -11.8) * mm, "mid": v(-59.28, -10.09) * mm, "end": v(-60.3, -8.71) * mm});
            skPoint(sketch, "E220.visualSharp", {"position": v(-60.86, -15.4) * mm});
            skArc(sketch, "E220.filletArc", {"start": v(-63.53, -14) * mm, "mid": v(-61.4, -14.3) * mm, "end": v(-59.8, -12.84) * mm});
            skPoint(sketch, "E221.visualSharp", {"position": v(-69.88, -6.38) * mm});
            skArc(sketch, "E221.filletArc", {"start": v(-67.32, -5.32) * mm, "mid": v(-68.78, -6.9) * mm, "end": v(-68.49, -9.04) * mm});
            skCircle(sketch, "E222", {"center": v(-111.63, 0) * mm, "radius": 10.48 * mm, "construction": true});
            skCircle(sketch, "E223", {"center": v(-111.63, 0) * mm, "radius": 16.67 * mm, "construction": true});
            skLineSegment(sketch, "E224", {"start": v(-105.25, 15.4) * mm, "end": v(-118.01, -15.4) * mm, "construction": true});
            skLineSegment(sketch, "E225", {"start": v(-118.01, 15.4) * mm, "end": v(-105.25, -15.4) * mm, "construction": true});
            skLineSegment(sketch, "E226", {"start": v(-127.03, 6.38) * mm, "end": v(-96.23, -6.38) * mm, "construction": true});
            skLineSegment(sketch, "E227", {"start": v(-96.23, 6.38) * mm, "end": v(-127.03, -6.38) * mm, "construction": true});
            skLineSegment(sketch, "E228", {"start": v(-128.3, 0) * mm, "end": v(-94.96, 0) * mm, "construction": true});
            skLineSegment(sketch, "E229", {"start": v(-116.52, -11.8) * mm, "end": v(-116.95, -12.84) * mm});
            skLineSegment(sketch, "E230", {"start": v(-123.43, -4.89) * mm, "end": v(-124.47, -5.32) * mm});
            skLineSegment(sketch, "E231", {"start": v(-123.43, 4.89) * mm, "end": v(-124.47, 5.32) * mm});
            skLineSegment(sketch, "E232", {"start": v(-116.52, 11.8) * mm, "end": v(-116.95, 12.84) * mm});
            skLineSegment(sketch, "E233", {"start": v(-106.75, 11.8) * mm, "end": v(-106.31, 12.84) * mm});
            skLineSegment(sketch, "E234", {"start": v(-99.84, 4.89) * mm, "end": v(-98.8, 5.32) * mm});
            skLineSegment(sketch, "E235", {"start": v(-101.16, 0) * mm, "end": v(-94.96, 0) * mm});
            skLineSegment(sketch, "E236", {"start": v(-99.84, -4.89) * mm, "end": v(-98.8, -5.32) * mm});
            skLineSegment(sketch, "E237", {"start": v(-106.75, -11.8) * mm, "end": v(-106.31, -12.84) * mm});
            skArc(sketch, "E238", {"start": v(-102.59, -14) * mm, "mid": v(-99.85, -11.79) * mm, "end": v(-97.63, -9.04) * mm});
            skArc(sketch, "E239", {"start": v(-97.63, 9.04) * mm, "mid": v(-99.85, 11.79) * mm, "end": v(-102.59, 14) * mm});
            skArc(sketch, "E240", {"start": v(-120.68, 14) * mm, "mid": v(-123.42, 11.79) * mm, "end": v(-125.64, 9.04) * mm});
            skArc(sketch, "E241", {"start": v(-125.64, -9.04) * mm, "mid": v(-123.42, -11.79) * mm, "end": v(-120.68, -14) * mm});
            skArc(sketch, "E242", {"start": v(-102.92, -5.82) * mm, "mid": v(-104.22, -7.4) * mm, "end": v(-105.81, -8.71) * mm});
            skArc(sketch, "E243", {"start": v(-117.45, -8.71) * mm, "mid": v(-119.04, -7.4) * mm, "end": v(-120.34, -5.82) * mm});
            skArc(sketch, "E244", {"start": v(-120.34, 5.82) * mm, "mid": v(-119.04, 7.4) * mm, "end": v(-117.45, 8.71) * mm});
            skArc(sketch, "E245", {"start": v(-105.81, 8.71) * mm, "mid": v(-104.22, 7.4) * mm, "end": v(-102.92, 5.82) * mm});
            skPoint(sketch, "E246.visualSharp", {"position": v(-107.62, -9.68) * mm});
            skArc(sketch, "E246.filletArc", {"start": v(-105.81, -8.71) * mm, "mid": v(-106.83, -10.09) * mm, "end": v(-106.75, -11.8) * mm});
            skPoint(sketch, "E247.visualSharp", {"position": v(-105.25, -15.4) * mm});
            skArc(sketch, "E247.filletArc", {"start": v(-106.31, -12.84) * mm, "mid": v(-104.72, -14.3) * mm, "end": v(-102.59, -14) * mm});
            skPoint(sketch, "E248.visualSharp", {"position": v(-96.23, -6.38) * mm});
            skArc(sketch, "E248.filletArc", {"start": v(-97.63, -9.04) * mm, "mid": v(-97.34, -6.9) * mm, "end": v(-98.8, -5.32) * mm});
            skPoint(sketch, "E249.visualSharp", {"position": v(-101.95, -4) * mm});
            skArc(sketch, "E249.filletArc", {"start": v(-99.84, -4.89) * mm, "mid": v(-101.55, -4.8) * mm, "end": v(-102.92, -5.82) * mm});
            skPoint(sketch, "E250.visualSharp", {"position": v(-101.95, 4) * mm});
            skArc(sketch, "E250.filletArc", {"start": v(-102.92, 5.82) * mm, "mid": v(-101.55, 4.8) * mm, "end": v(-99.84, 4.89) * mm});
            skPoint(sketch, "E251.visualSharp", {"position": v(-96.23, 6.38) * mm});
            skArc(sketch, "E251.filletArc", {"start": v(-98.8, 5.32) * mm, "mid": v(-97.34, 6.9) * mm, "end": v(-97.63, 9.04) * mm});
            skPoint(sketch, "E252.visualSharp", {"position": v(-105.25, 15.4) * mm});
            skArc(sketch, "E252.filletArc", {"start": v(-102.59, 14) * mm, "mid": v(-104.72, 14.3) * mm, "end": v(-106.31, 12.84) * mm});
            skPoint(sketch, "E253.visualSharp", {"position": v(-107.62, 9.68) * mm});
            skArc(sketch, "E253.filletArc", {"start": v(-106.75, 11.8) * mm, "mid": v(-106.83, 10.09) * mm, "end": v(-105.81, 8.71) * mm});
            skPoint(sketch, "E254.visualSharp", {"position": v(-115.64, 9.68) * mm});
            skArc(sketch, "E254.filletArc", {"start": v(-117.45, 8.71) * mm, "mid": v(-116.43, 10.09) * mm, "end": v(-116.52, 11.8) * mm});
            skPoint(sketch, "E255.visualSharp", {"position": v(-118.01, 15.4) * mm});
            skArc(sketch, "E255.filletArc", {"start": v(-116.95, 12.84) * mm, "mid": v(-118.54, 14.3) * mm, "end": v(-120.68, 14) * mm});
            skPoint(sketch, "E256.visualSharp", {"position": v(-127.03, 6.38) * mm});
            skArc(sketch, "E256.filletArc", {"start": v(-125.64, 9.04) * mm, "mid": v(-125.93, 6.9) * mm, "end": v(-124.47, 5.32) * mm});
            skPoint(sketch, "E257.visualSharp", {"position": v(-121.31, 4) * mm});
            skArc(sketch, "E257.filletArc", {"start": v(-123.43, 4.89) * mm, "mid": v(-121.72, 4.8) * mm, "end": v(-120.34, 5.82) * mm});
            skPoint(sketch, "E258.visualSharp", {"position": v(-121.31, -4) * mm});
            skArc(sketch, "E258.filletArc", {"start": v(-120.34, -5.82) * mm, "mid": v(-121.72, -4.8) * mm, "end": v(-123.43, -4.89) * mm});
            skPoint(sketch, "E259.visualSharp", {"position": v(-115.64, -9.68) * mm});
            skArc(sketch, "E259.filletArc", {"start": v(-116.52, -11.8) * mm, "mid": v(-116.43, -10.09) * mm, "end": v(-117.45, -8.71) * mm});
            skPoint(sketch, "E260.visualSharp", {"position": v(-118.01, -15.4) * mm});
            skArc(sketch, "E260.filletArc", {"start": v(-120.68, -14) * mm, "mid": v(-118.54, -14.3) * mm, "end": v(-116.95, -12.84) * mm});
            skPoint(sketch, "E261.visualSharp", {"position": v(-127.03, -6.38) * mm});
            skArc(sketch, "E261.filletArc", {"start": v(-124.47, -5.32) * mm, "mid": v(-125.93, -6.9) * mm, "end": v(-125.64, -9.04) * mm});
            skSolve(sketch);
        }
        {
            var Q0;
            Q0 = qSketchRegion(id + "F14", true);
            extrude(context, id + "F15", {"entities" : qUnion([Q0]), "operationType" : NewBodyOperationType.REMOVE, "oppositeDirection" : true, "depth" : 25.4 * mm, "offsetDistance" : 25.4 * mm});
        }
    });
